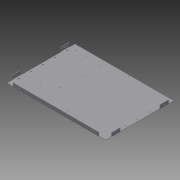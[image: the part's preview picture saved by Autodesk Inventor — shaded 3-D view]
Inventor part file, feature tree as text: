
AUTODESK INVENTOR PART (.ipt)
format: ipt  version: 2013 SP2 (Build 170200200, 200)  size: 348,160 bytes
history: native  units: mm
features: sketch x10, sheet_metal_op x7, hole x7, other x4, mirror x3, plane x2, projected_geometry x2
ambient origin geometry x8: Origin, YZ Plane, XZ Plane, XY Plane, X Axis, Y Axis, Z Axis, Center Point
bodies: Solid1 (feature_tree)
feature tree (35):
  sheet_metal_op  "Face1"
  sheet_metal_op  "Flange1"
  hole  "Hole1"  [1 undecoded]
  plane  "Work Plane1"
  mirror  "Mirror1"
  plane  "Work Plane2"
  mirror  "Mirror2"
  hole  "Hole2"  [1 undecoded]
  hole  "Hole3"  [1 undecoded]
  hole  "Hole4"  [1 undecoded]
  sheet_metal_op  "Flange2"
  hole  "Hole5"  [1 undecoded]
  hole  "Hole6"  [1 undecoded]
  hole  "Hole8"  [1 undecoded]
  mirror  "Mirror3"
  sketch  "Sketch1"  dims[d0=458.0mm d2=315.0mm]
  other  "Plate1"
  sketch  "Sketch2"  dims[d3=1.5mm d4=1.5mm]
  other  "Plate2"
  sheet_metal_op  "Bend1"
  sheet_metal_op  "Corner1"
  sketch  "Sketch3"  dims[d5=0.75mm d6=3.0mm]
  projected_geometry  "Projected Loop1"
  sketch  "Sketch4"  dims[d7=1.5mm d8=18.0mm d9=90.0deg d10=1.5mm]
  sketch  "Sketch5"  dims[d11=40.0mm d12=25.0mm d13=6.0mm]
  sketch  "Sketch6"  dims[d14=1.5mm d15=1.5mm]
  sketch  "Sketch7"  dims[d16=10.0mm]
  other  "Plate3"
  sheet_metal_op  "Bend2"
  sheet_metal_op  "Corner2"
  sketch  "Sketch8"  dims[d17=4.5mm d18=6.0mm d19=4.0mm d20=2.0mm d21=90.0deg d22=1.5mm d23=20.594885mm]
  projected_geometry  "Projected Loop2"
  sketch  "Sketch9"  dims[d24=47.0mm]
  sketch  "Sketch11"  dims[d25=213.0mm d26=30.0mm d27=25.0mm d28=3.4mm d29=6.0mm d30=4.0mm d31=2.0mm d32=90.0deg d33=1.5mm d34=20.594885mm d35=78.0mm d36=3.4mm d37=6.0mm d38=4.0mm d39=2.0mm d40=90.0deg d41=1.5mm d42=20.594885mm d43=180.0mm d44=294.0mm d45=27.0mm d46=8.5mm d47=12.0mm d49=29.5mm d50=7.0mm d51=0.0mm d52=50.0mm d53=3.4mm d54=6.0mm d55=4.0mm d56=2.0mm d57=90.0deg d58=1.5mm d59=20.594885mm d60=117.0mm d61=1.5mm d62=0.75mm d63=3.0mm d64=1.5mm d65=18.0mm d66=90.0deg d67=1.5mm d68=398.0mm d69=6.0mm d70=1.5mm d71=1.5mm d72=10.0mm d73=4.5mm d74=6.0mm d75=4.0mm d76=2.0mm d77=90.0deg d78=1.5mm d79=20.594885mm d80=100.0mm d81=4.5mm d82=6.0mm d83=4.0mm d84=2.0mm d85=90.0deg d86=1.5mm d87=20.594885mm d88=30.0mm d90=10.0mm d91=30.0mm d92=144.0mm d93=32.0mm d106=9.0mm d107=5.5mm d108=6.0mm d109=4.0mm d110=2.0mm d111=90.0deg d112=1.5mm d113=20.594885mm]
  other  "Definition1"
note: 7 required parameter values undecoded (feature->parameter linkage not recoverable at this tier; creation-order binding heuristic only, values carry confidence <= 0.55)
